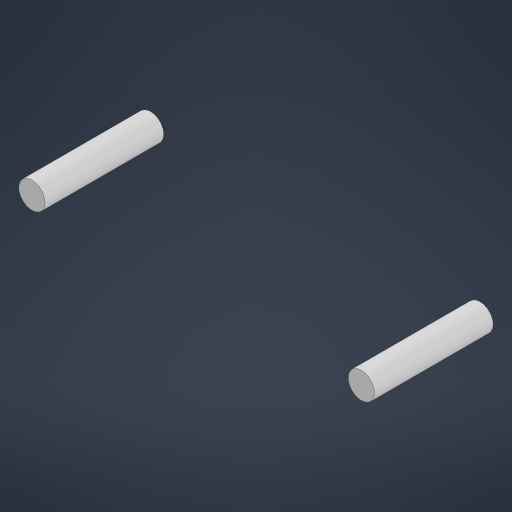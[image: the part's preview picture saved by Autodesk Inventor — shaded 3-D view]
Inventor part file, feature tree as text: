
AUTODESK INVENTOR PART (.ipt)
format: ipt  version: 2024 (Build 280153000, 153)  size: 177,152 bytes
history: native  units: mm
features: other x5, plane x1, extrude x1, sketch x1
ambient origin geometry x8: Origin, YZ Plane, XZ Plane, XY Plane, X Axis, Y Axis, Z Axis, Center Point
bodies: Body1 (feature_tree)
feature tree (8):
  other  "Sólido1"
  plane  "Plano de trabajo1"
  extrude  "Extrusión1"  Depth=18.0mm
  sketch  "Boceto1"  dims[d2=5.0mm d3=5.0mm d4=124.2mm d5=50.0mm d6=18.0mm d7=0.0mm]
  other  "<userpath>\Downloads\Piezas CMR\Marco_APM_002\Marco_apm_002-2.iam"
  other  "Marco_apm_002-2.iam"
  other  "Marco_Conveyor_Aereo:1"
  other  "Marco:1"
